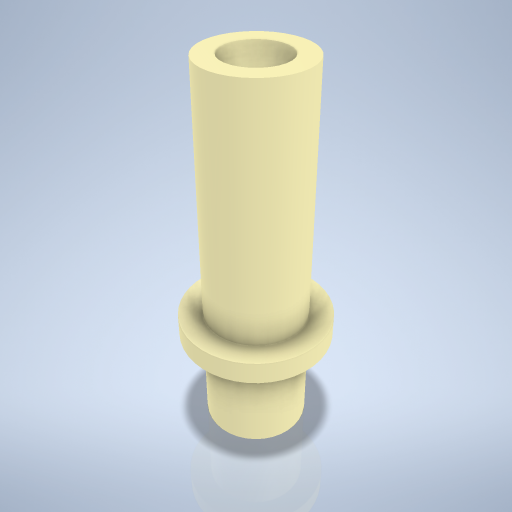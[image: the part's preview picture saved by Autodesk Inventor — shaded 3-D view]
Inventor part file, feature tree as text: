
AUTODESK INVENTOR PART (.ipt)
format: ipt  version: 2024.2 (Build 282272000, 272)  size: 274,432 bytes
history: native  units: mm
features: sketch x2, revolve x1, hole x1
ambient origin geometry x8: Origin, YZ Plane, XZ Plane, XY Plane, X Axis, Y Axis, Z Axis, Center Point
bodies: Volumenkörper1 (feature_tree)
feature tree (4):
  revolve  "Umdrehung1"
  hole  "Bohrung1"  [1 undecoded]
  sketch  "Skizze1"  dims[d0=6.5mm d1=9.5mm]
  sketch  "Skizze2"  dims[d2=16.0mm d3=1.5mm d4=6.5mm d5=90.0deg d6=4.0mm d7=6.0mm d8=4.0mm d9=2.0mm d10=90.0deg d11=8.0mm d12=0.0mm]
note: 1 required parameter value undecoded (feature->parameter linkage not recoverable at this tier; creation-order binding heuristic only, values carry confidence <= 0.55)
